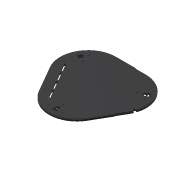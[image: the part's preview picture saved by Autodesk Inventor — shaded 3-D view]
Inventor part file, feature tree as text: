
AUTODESK INVENTOR PART (.ipt)
format: ipt  version: 2016 (Build 200138000, 138)  size: 600,064 bytes
history: native  units: mm
features: sketch x14, extrude x13, thread x4, hole x4, fillet x2, pattern_circular x2, reference x2, projected_geometry x2
ambient origin geometry x8: Origin, YZ Plane, XZ Plane, XY Plane, X Axis, Y Axis, Z Axis, Center Point
bodies: Solid1 (feature_tree)
feature tree (43):
  extrude  "Extrusion1"  Depth=8.0mm
  extrude  "Extrusion2"  Depth=2.5mm
  extrude  "Extrusion3"  Depth=6.4mm
  fillet  "Fillet1"  Radius=20.0mm
  extrude  "Extrusion4"  Depth=18.0mm
  pattern_circular  "Circular Pattern1"  [2 undecoded]
  extrude  "Extrusion6"  Depth=3.0mm
  extrude  "Extrusion7"  Depth=10.0mm TaperAngle=0.0deg
  extrude  "Extrusion8"  Depth=4.0mm
  extrude  "Extrusion9"  Depth=6.5mm
  thread  "Thread1"  [1 undecoded]
  thread  "Thread2"  [1 undecoded]
  thread  "Thread3"  [1 undecoded]
  thread  "Thread4"  [1 undecoded]
  extrude  "Extrusion11"  Depth=2.5mm
  extrude  "Extrusion12"  Depth=4.0mm
  hole  "Hole1"  [1 undecoded]
  hole  "Hole2"  [1 undecoded]
  hole  "Hole3"  [1 undecoded]
  extrude  "Extrusion14"  Depth=8.0mm TaperAngle=360.0deg
  hole  "Hole4"  [1 undecoded]
  pattern_circular  "Circular Pattern2"  [2 undecoded]
  extrude  "Extrusion15"  Depth=3.0mm TaperAngle=0.0deg
  fillet  "Fillet2"  Radius=1.5mm
  extrude  "Extrusion16"  Depth=6.0mm
  sketch  "Sketch1"  dims[d0=8.0mm d1=0.0mm d2=24.0mm]
  reference  "Reference1"
  sketch  "Sketch2"  dims[d3=24.0mm d4=2.5mm]
  projected_geometry  "Projected Loop1"
  sketch  "Sketch3"  dims[d5=7.0mm d6=3.7mm d7=6.4mm d8=20.0mm]
  sketch  "Sketch4"  dims[d9=18.0mm d10=18.0mm]
  sketch  "Sketch6"  dims[d11=3.7mm]
  sketch  "Sketch7"  dims[d12=6.4mm]
  sketch  "Sketch8"  dims[d13=0.7mm]
  projected_geometry  "Projected Loop2"
  sketch  "Sketch9"  dims[d14=0.7mm]
  sketch  "Sketch11"  dims[d15=14.0mm]
  sketch  "Sketch12"  dims[d16=21.0mm]
  sketch  "Sketch14"  dims[d17=3.0mm]
  reference  "Reference2"
  sketch  "Sketch16"  dims[d18=1.5mm]
  sketch  "Sketch17"  dims[d19=1.5mm]
  sketch  "Sketch18"  dims[d20=1.5mm d21=3.0mm d22=3.0mm d23=10.0mm d24=0.0mm d25=4.0mm d26=6.5mm d28=4.0mm d29=0.0mm d30=2.0mm d31=12.0mm d32=2.5mm d33=2.5mm d34=4.0mm d35=15.0mm d36=15.0mm d37=2.4mm d38=0.0mm d39=30.0mm d40=360.0deg d45=3.2mm d46=1.0mm d47=0.0mm d48=3.0mm d49=0.0mm d50=1.5mm d51=6.0mm d52=6.0mm d53=10.0mm d54=0.0mm d55=3.2mm d56=23.0mm d57=3.2mm d58=23.0mm d59=1.7mm d60=0.0mm d61=0.0mm d62=3.25mm d63=3.25mm d64=5.8mm d65=5.8mm d66=6.0mm d67=6.0mm d68=15.0mm d69=0.0mm d70=3.25mm d71=3.25mm d72=5.8mm d73=5.8mm d74=6.0mm d75=32.5mm d76=10.0mm d77=0.0mm d78=10.0mm d79=0.0mm d80=10.0mm d81=0.0mm d82=10.0mm d83=0.0mm d87=10.0mm d88=20.0mm d89=20.0mm d90=0.0mm d91=240.0mm d92=7.5mm d93=7.5mm d94=7.5mm d95=2.0mm d96=0.0mm d97=10.0mm d98=10.0mm d99=3.0mm d100=6.0mm d101=4.0mm d102=2.0mm d103=90.0deg d104=8.0mm d105=20.594885mm d106=10.0mm d107=10.0mm d108=3.0mm d109=6.0mm d110=4.0mm d111=2.0mm d112=90.0deg d113=8.0mm d114=20.594885mm d115=10.0mm d116=10.0mm d117=3.0mm d118=6.0mm d119=4.0mm d120=2.0mm d121=90.0deg d122=8.0mm d123=20.594885mm d144=10.0mm d145=0.0mm d146=3.0mm d147=5.0mm d148=2.459mm d149=4.0mm d150=4.0mm d151=2.0mm d152=90.0deg d153=7.0mm d154=20.594885mm d155=30.0mm d156=360.0deg d162=6.0mm d163=190.0mm d164=9.5mm d165=9.0mm d166=9.5mm d167=40.5mm d168=40.5mm d169=40.5mm d170=35.0mm d171=10.0mm d172=0.0mm d173=2.0mm d174=8.0mm d175=0.0mm]
note: 12 required parameter values undecoded (feature->parameter linkage not recoverable at this tier; creation-order binding heuristic only, values carry confidence <= 0.55)
